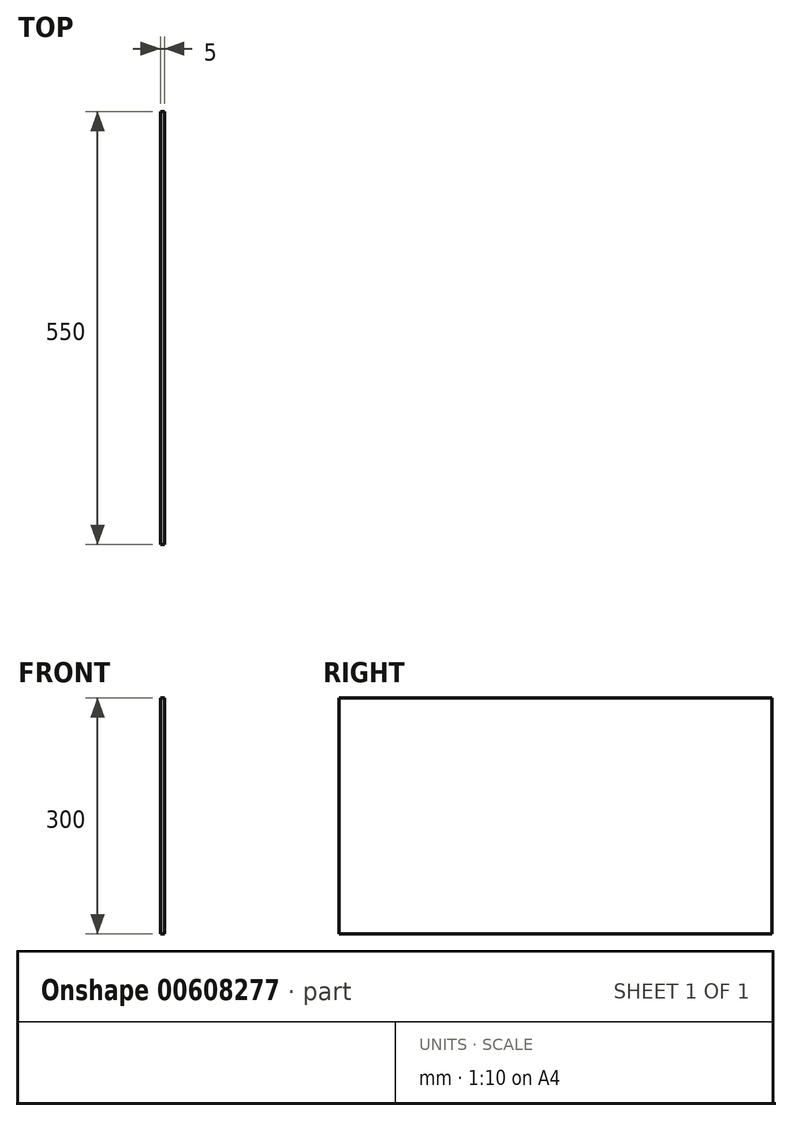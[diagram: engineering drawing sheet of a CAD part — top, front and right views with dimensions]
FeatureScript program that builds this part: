
annotation { "Feature Type Name" : "Feature", "Feature Type Description" : "" }
export const myFeature = defineFeature(function(context is Context, id is Id, definition is map)
    precondition{}
    {
        {
            var Q0;
            Q0=qCreatedBy(makeId("Right.planeOp"),FACE);
            var sketch = newSketch(context, id + "F0", { "sketchPlane" : qUnion([Q0])});
            skLineSegment(sketch, "E0.bottom", {"start": v(275, 150) * mm, "end": v(-275, 150) * mm});
            skLineSegment(sketch, "E0.top", {"start": v(275, -150) * mm, "end": v(-275, -150) * mm});
            skLineSegment(sketch, "E0.left", {"start": v(275, 150) * mm, "end": v(275, -150) * mm});
            skLineSegment(sketch, "E0.right", {"start": v(-275, 150) * mm, "end": v(-275, -150) * mm});
            skPoint(sketch, "E0.middle", {"position": v(0, 0) * mm});
            skSolve(sketch);
        }
        {
            var Q0;
            Q0 = qSketchRegion(id + "F0", true);
            extrude(context, id + "F1", {"entities" : qUnion([Q0]), "depth" : 5 * mm, "offsetDistance" : 25 * mm});
        }
    });
